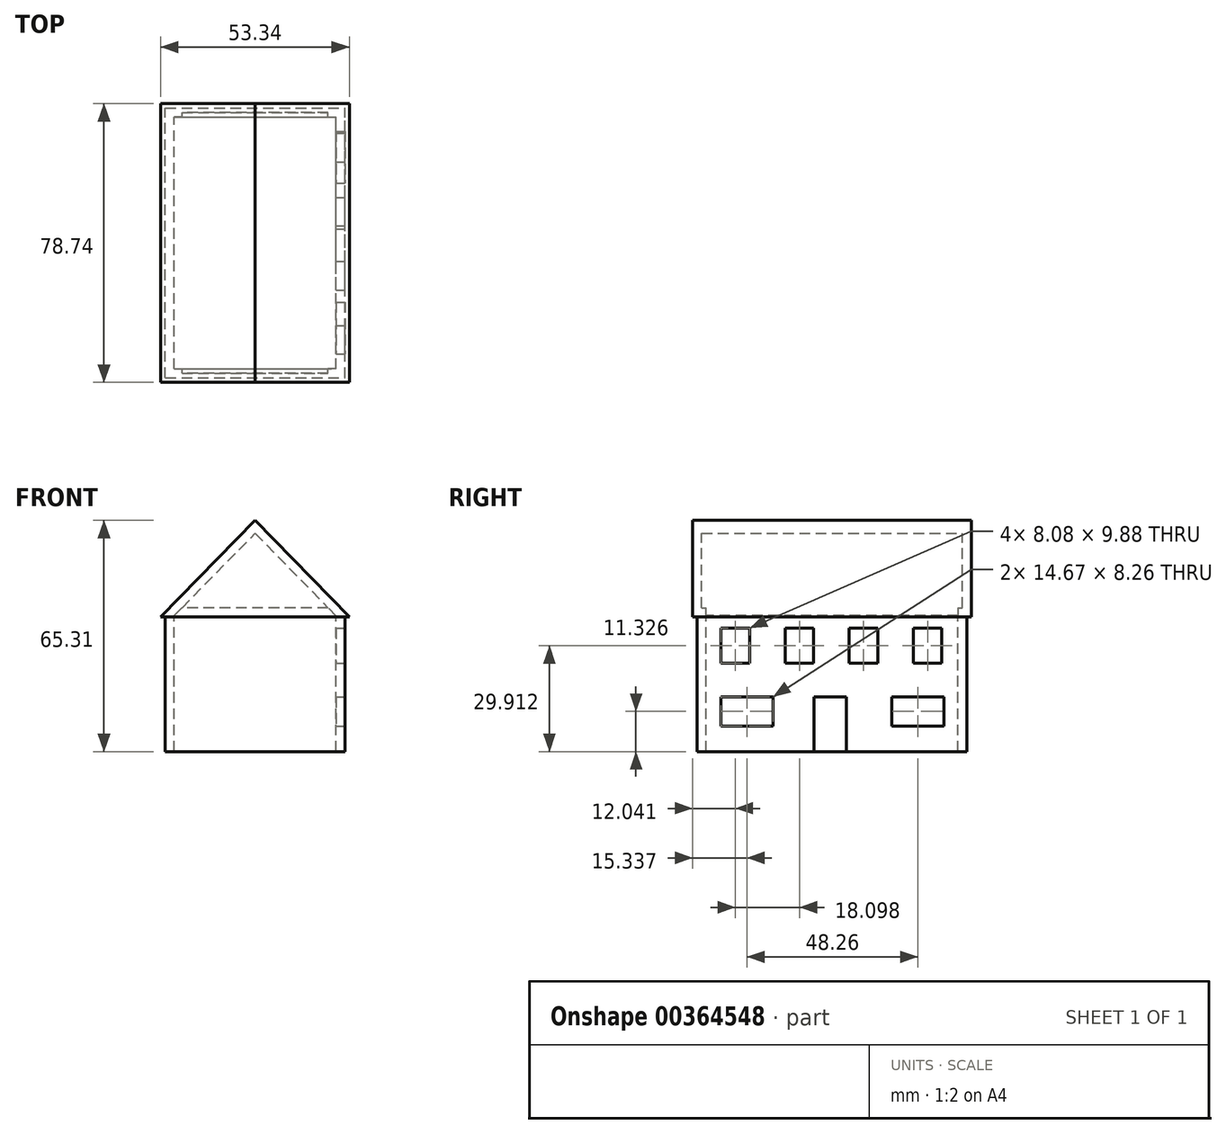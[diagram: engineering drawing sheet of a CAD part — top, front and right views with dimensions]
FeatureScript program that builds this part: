
annotation { "Feature Type Name" : "Feature", "Feature Type Description" : "" }
export const myFeature = defineFeature(function(context is Context, id is Id, definition is map)
    precondition{}
    {
        {
            var Q0;
            Q0=qCreatedBy(makeId("Front.planeOp"),FACE);
            var sketch = newSketch(context, id + "F0", { "sketchPlane" : qUnion([Q0])});
            skLineSegment(sketch, "E0.bottom", {"start": v(-25.4, 0) * mm, "end": v(25.4, 0) * mm});
            skLineSegment(sketch, "E0.top", {"start": v(-25.4, 38.1) * mm, "end": v(25.4, 38.1) * mm});
            skLineSegment(sketch, "E0.left", {"start": v(-25.4, 0) * mm, "end": v(-25.4, 38.1) * mm});
            skLineSegment(sketch, "E0.right", {"start": v(25.4, 0) * mm, "end": v(25.4, 38.1) * mm});
            skSolve(sketch);
        }
        {
            var Q0;
            Q0=qCreatedBy(makeId("Front.planeOp"),FACE);
            var sketch = newSketch(context, id + "F1", { "sketchPlane" : qUnion([Q0])});
            skLineSegment(sketch, "E1", {"start": v(-26.75, 38.1) * mm, "end": v(0, 65.31) * mm});
            skLineSegment(sketch, "E2", {"start": v(0, 65.31) * mm, "end": v(26.59, 38.1) * mm});
            skLineSegment(sketch, "E3", {"start": v(26.59, 38.1) * mm, "end": v(-26.75, 38.1) * mm});
            skSolve(sketch);
        }
        {
            var Q0;
            Q0=makeQuery(id+"F0.imprint","IMPRINT",FACE,{"disambiguationData":[TD([[makeQuery(id+"F0.imprint","IMPRINT",EDGE,{"derivedFrom":sQuery(id+"F0.wireOp",EDGE,"E0.bottom")}),1.0]])]});
            extrude(context, id + "F2", {"entities" : qUnion([Q0]), "depth" : 38.1 * mm, "hasSecondDirection" : true, "secondDirectionOppositeDirection" : true, "secondDirectionDepth" : 38.1 * mm});
        }
        {
            var Q0;
            Q0=makeQuery(id+"F1.imprint","IMPRINT",FACE,{"disambiguationData":[TD([[makeQuery(id+"F1.imprint","IMPRINT",EDGE,{"derivedFrom":sQuery(id+"F1.wireOp",EDGE,"E1")}),-1.0]])]});
            extrude(context, id + "F3", {"entities" : qUnion([Q0]), "operationType" : NewBodyOperationType.ADD, "depth" : 39.37 * mm, "hasSecondDirection" : true, "secondDirectionOppositeDirection" : true, "secondDirectionDepth" : 39.37 * mm});
        }
        {
            var Q0;
            Q0=makeQuery(id+"F2.opExtrude","SWEPT_FACE",FACE,{"disambiguationData":[OSD([sQuery(id+"F0.wireOp",EDGE,"E0.bottom")])]});
            shell(context, id + "F4", {"entities" : qUnion([Q0]), "thickness" : 2.54 * mm});
        }
        {
            var Q0;
            Q0=makeQuery(id+"F2.opExtrude","SWEPT_FACE",FACE,{"disambiguationData":[OSD([sQuery(id+"F0.wireOp",EDGE,"E0.right")])]});
            cPlane(context, id + "F5", {"entities" : qUnion([Q0]), "cplaneType" : CPlaneType.OFFSET, "offset" : 0 * mm, "width" : 152.4 * mm, "height" : 152.4 * mm});
        }
        {
            var Q0;
            Q0=qCreatedBy(id+"F5.planeOp",FACE);
            var sketch = newSketch(context, id + "F6", { "sketchPlane" : qUnion([Q0])});
            skLineSegment(sketch, "E4.bottom", {"start": v(-5.1, 0) * mm, "end": v(4.04, 0) * mm});
            skLineSegment(sketch, "E4.top", {"start": v(-5.1, 15.45) * mm, "end": v(4.04, 15.45) * mm});
            skLineSegment(sketch, "E4.left", {"start": v(-5.1, 0) * mm, "end": v(-5.1, 15.45) * mm});
            skLineSegment(sketch, "E4.right", {"start": v(4.04, 0) * mm, "end": v(4.04, 15.45) * mm});
            skLineSegment(sketch, "E5.bottom", {"start": v(-16.7, 15.45) * mm, "end": v(-31.37, 15.45) * mm});
            skLineSegment(sketch, "E5.top", {"start": v(-16.7, 7.2) * mm, "end": v(-31.37, 7.2) * mm});
            skLineSegment(sketch, "E5.left", {"start": v(-16.7, 15.45) * mm, "end": v(-16.7, 7.2) * mm});
            skLineSegment(sketch, "E5.right", {"start": v(-31.37, 15.45) * mm, "end": v(-31.37, 7.2) * mm});
            skLineSegment(sketch, "E6.bottom", {"start": v(-31.37, 34.85) * mm, "end": v(-23.29, 34.85) * mm});
            skLineSegment(sketch, "E6.top", {"start": v(-31.37, 24.97) * mm, "end": v(-23.29, 24.97) * mm});
            skLineSegment(sketch, "E6.left", {"start": v(-31.37, 34.85) * mm, "end": v(-31.37, 24.97) * mm});
            skLineSegment(sketch, "E6.right", {"start": v(-23.29, 34.85) * mm, "end": v(-23.29, 24.97) * mm});
            skLineSegment(sketch, "E7.1.0.0", {"start": v(-13.27, 34.85) * mm, "end": v(-13.27, 24.97) * mm});
            skLineSegment(sketch, "E7.1.0.1", {"start": v(-13.27, 24.97) * mm, "end": v(-5.2, 24.97) * mm});
            skLineSegment(sketch, "E7.1.0.2", {"start": v(-5.2, 34.85) * mm, "end": v(-5.2, 24.97) * mm});
            skLineSegment(sketch, "E7.1.0.3", {"start": v(-13.27, 34.85) * mm, "end": v(-5.2, 34.85) * mm});
            skLineSegment(sketch, "E7.2.0.0", {"start": v(4.83, 34.85) * mm, "end": v(4.83, 24.97) * mm});
            skLineSegment(sketch, "E7.2.0.1", {"start": v(4.83, 24.97) * mm, "end": v(12.9, 24.97) * mm});
            skLineSegment(sketch, "E7.2.0.2", {"start": v(12.9, 34.85) * mm, "end": v(12.9, 24.97) * mm});
            skLineSegment(sketch, "E7.2.0.3", {"start": v(4.83, 34.85) * mm, "end": v(12.9, 34.85) * mm});
            skLineSegment(sketch, "E7.3.0.0", {"start": v(22.92, 34.85) * mm, "end": v(22.92, 24.97) * mm});
            skLineSegment(sketch, "E7.3.0.1", {"start": v(22.92, 24.97) * mm, "end": v(31, 24.97) * mm});
            skLineSegment(sketch, "E7.3.0.2", {"start": v(31, 34.85) * mm, "end": v(31, 24.97) * mm});
            skLineSegment(sketch, "E7.3.0.3", {"start": v(22.92, 34.85) * mm, "end": v(31, 34.85) * mm});
            skLineSegment(sketch, "E7.direction1", {"start": v(-31.37, 24.97) * mm, "end": v(-13.27, 24.97) * mm, "construction": true});
            skLineSegment(sketch, "E8.1.0.0", {"start": v(31.56, 7.2) * mm, "end": v(16.9, 7.2) * mm});
            skLineSegment(sketch, "E8.1.0.1", {"start": v(31.56, 15.45) * mm, "end": v(31.56, 7.2) * mm});
            skLineSegment(sketch, "E8.1.0.2", {"start": v(31.56, 15.45) * mm, "end": v(16.9, 15.45) * mm});
            skLineSegment(sketch, "E8.1.0.3", {"start": v(16.9, 15.45) * mm, "end": v(16.9, 7.2) * mm});
            skLineSegment(sketch, "E8.direction1", {"start": v(-31.37, 7.2) * mm, "end": v(16.9, 7.2) * mm, "construction": true});
            skSolve(sketch);
        }
        {
            var Q0;
            Q0=makeQuery(id+"F6.imprint","IMPRINT",FACE,{"disambiguationData":[TD([[makeQuery(id+"F6.imprint","IMPRINT",EDGE,{"derivedFrom":sQuery(id+"F6.wireOp",EDGE,"E4.bottom")}),1.0]])]});
            var Q1;
            Q1=makeQuery(id+"F6.imprint","IMPRINT",FACE,{"disambiguationData":[TD([[makeQuery(id+"F6.imprint","IMPRINT",EDGE,{"derivedFrom":sQuery(id+"F6.wireOp",EDGE,"E6.bottom")}),-1.0]])]});
            var Q2;
            Q2=makeQuery(id+"F6.imprint","IMPRINT",FACE,{"disambiguationData":[TD([[makeQuery(id+"F6.imprint","IMPRINT",EDGE,{"derivedFrom":sQuery(id+"F6.wireOp",EDGE,"E7.1.0.0")}),1.0]])]});
            var Q3;
            Q3=makeQuery(id+"F6.imprint","IMPRINT",FACE,{"disambiguationData":[TD([[makeQuery(id+"F6.imprint","IMPRINT",EDGE,{"derivedFrom":sQuery(id+"F6.wireOp",EDGE,"E7.2.0.0")}),1.0]])]});
            var Q4;
            Q4=makeQuery(id+"F6.imprint","IMPRINT",FACE,{"disambiguationData":[TD([[makeQuery(id+"F6.imprint","IMPRINT",EDGE,{"derivedFrom":sQuery(id+"F6.wireOp",EDGE,"E7.3.0.0")}),1.0]])]});
            var Q5;
            Q5=makeQuery(id+"F6.imprint","IMPRINT",FACE,{"disambiguationData":[TD([[makeQuery(id+"F6.imprint","IMPRINT",EDGE,{"derivedFrom":sQuery(id+"F6.wireOp",EDGE,"E8.1.0.0")}),-1.0]])]});
            var Q6;
            Q6=makeQuery(id+"F6.imprint","IMPRINT",FACE,{"disambiguationData":[TD([[makeQuery(id+"F6.imprint","IMPRINT",EDGE,{"derivedFrom":sQuery(id+"F6.wireOp",EDGE,"E5.bottom")}),1.0]])]});
            extrude(context, id + "F7", {"entities" : qUnion([Q0, Q1, Q2, Q3, Q4, Q5, Q6]), "operationType" : NewBodyOperationType.REMOVE, "oppositeDirection" : true, "depth" : 2.54 * mm});
        }
        {
            var Q0;
            Q0=qCreatedBy(id+"F5.planeOp",FACE);
            var sketch = newSketch(context, id + "F8", { "sketchPlane" : qUnion([Q0])});
            skLineSegment(sketch, "E9", {"start": v(-27.33, 34.85) * mm, "end": v(-27.33, 24.97) * mm});
            skLineSegment(sketch, "E10", {"start": v(-23.29, 29.91) * mm, "end": v(-31.37, 29.91) * mm});
            skPoint(sketch, "E10.startSnap0", {"position": v(-27.33, 29.91) * mm});
            skLineSegment(sketch, "E11.1.0.0", {"start": v(-5.2, 29.91) * mm, "end": v(-13.27, 29.91) * mm});
            skLineSegment(sketch, "E11.1.0.1", {"start": v(-9.23, 34.85) * mm, "end": v(-9.23, 24.97) * mm});
            skLineSegment(sketch, "E11.2.0.0", {"start": v(12.9, 29.91) * mm, "end": v(4.83, 29.91) * mm});
            skLineSegment(sketch, "E11.2.0.1", {"start": v(8.87, 34.85) * mm, "end": v(8.87, 24.97) * mm});
            skLineSegment(sketch, "E11.3.0.0", {"start": v(31, 29.91) * mm, "end": v(22.92, 29.91) * mm});
            skLineSegment(sketch, "E11.3.0.1", {"start": v(26.96, 34.85) * mm, "end": v(26.96, 24.97) * mm});
            skLineSegment(sketch, "E11.direction1", {"start": v(-27.33, 24.97) * mm, "end": v(-9.23, 24.97) * mm, "construction": true});
            skSolve(sketch);
        }
        {
            var Q0;
            Q0=sQuery(id+"F8.wireOp",EDGE,"E9");
            extrude(context, id + "F9", {"bodyType" : ToolBodyType.SURFACE, "surfaceEntities" : qUnion([Q0]), "oppositeDirection" : true, "depth" : 2.54 * mm});
        }
        {
            var Q0;
            Q0=sQuery(id+"F8.wireOp",EDGE,"E10");
            extrude(context, id + "F10", {"bodyType" : ToolBodyType.SURFACE, "surfaceEntities" : qUnion([Q0]), "oppositeDirection" : true, "depth" : 2.54 * mm});
        }
        {
            var Q0;
            Q0=sQuery(id+"F8.wireOp",EDGE,"E11.1.0.1");
            var Q1;
            Q1=sQuery(id+"F8.wireOp",EDGE,"E11.2.0.1");
            var Q2;
            Q2=sQuery(id+"F8.wireOp",EDGE,"E11.3.0.1");
            extrude(context, id + "F11", {"bodyType" : ToolBodyType.SURFACE, "surfaceEntities" : qUnion([Q0, Q1, Q2]), "oppositeDirection" : true, "depth" : 2.54 * mm});
        }
        {
            var Q0;
            Q0=sQuery(id+"F8.wireOp",EDGE,"E11.1.0.0");
            var Q1;
            Q1=sQuery(id+"F8.wireOp",EDGE,"E11.2.0.0");
            var Q2;
            Q2=sQuery(id+"F8.wireOp",EDGE,"E11.3.0.0");
            extrude(context, id + "F12", {"bodyType" : ToolBodyType.SURFACE, "surfaceEntities" : qUnion([Q0, Q1, Q2]), "oppositeDirection" : true, "depth" : 2.54 * mm});
        }
        {
            var Q0;
            Q0=qCreatedBy(id+"F5.planeOp",FACE);
            var sketch = newSketch(context, id + "F13", { "sketchPlane" : qUnion([Q0])});
            skLineSegment(sketch, "E12", {"start": v(-24.03, 15.45) * mm, "end": v(-24.03, 7.16) * mm});
            skLineSegment(sketch, "E13", {"start": v(-16.7, 11.33) * mm, "end": v(-31.42, 11.33) * mm});
            skLineSegment(sketch, "E14.1.0.0", {"start": v(31.6, 11.33) * mm, "end": v(16.9, 11.33) * mm});
            skLineSegment(sketch, "E14.1.0.1", {"start": v(24.28, 15.45) * mm, "end": v(24.28, 7.16) * mm});
            skSolve(sketch);
        }
        {
            var Q0;
            Q0=sQuery(id+"F13.wireOp",EDGE,"E14.1.0.1");
            var Q1;
            Q1=sQuery(id+"F13.wireOp",EDGE,"E12");
            extrude(context, id + "F14", {"bodyType" : ToolBodyType.SURFACE, "surfaceEntities" : qUnion([Q0, Q1]), "oppositeDirection" : true, "depth" : 2.54 * mm});
        }
        {
            var Q0;
            Q0=sQuery(id+"F13.wireOp",EDGE,"E14.1.0.0");
            extrude(context, id + "F15", {"bodyType" : ToolBodyType.SURFACE, "surfaceEntities" : qUnion([Q0]), "oppositeDirection" : true, "depth" : 2.54 * mm});
        }
        {
            var Q0;
            Q0=sQuery(id+"F13.wireOp",EDGE,"E13");
            extrude(context, id + "F16", {"bodyType" : ToolBodyType.SURFACE, "surfaceEntities" : qUnion([Q0]), "oppositeDirection" : true, "depth" : 2.54 * mm});
        }
    });
